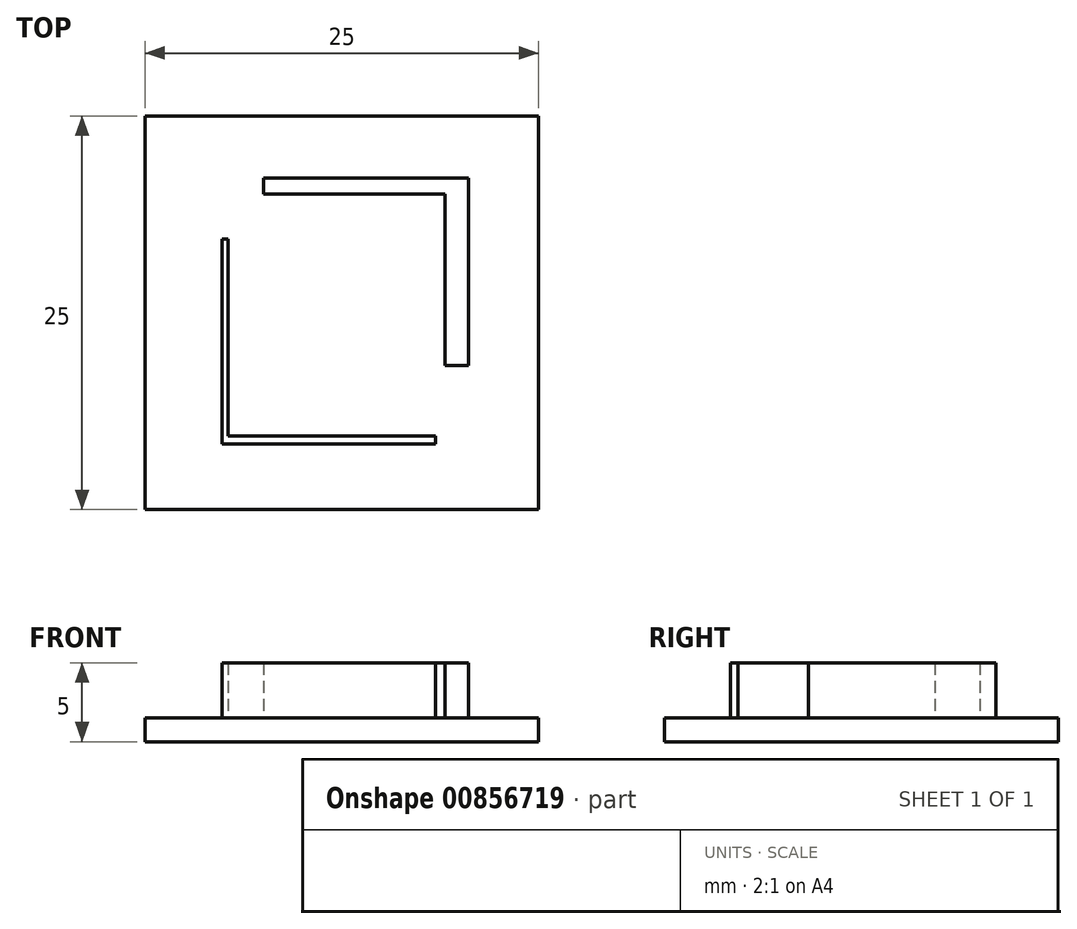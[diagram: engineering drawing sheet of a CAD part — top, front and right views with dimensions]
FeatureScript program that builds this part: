
annotation { "Feature Type Name" : "Feature", "Feature Type Description" : "" }
export const myFeature = defineFeature(function(context is Context, id is Id, definition is map)
    precondition{}
    {
        {
            var Q0;
            Q0=qCreatedBy(makeId("Top.planeOp"),FACE);
            var sketch = newSketch(context, id + "F0", { "sketchPlane" : qUnion([Q0])});
            skLineSegment(sketch, "E0.bottom", {"start": v(-25, 12.5) * mm, "end": v(0, 12.5) * mm});
            skLineSegment(sketch, "E0.top", {"start": v(-25, -12.5) * mm, "end": v(0, -12.5) * mm});
            skLineSegment(sketch, "E0.left", {"start": v(-25, 12.5) * mm, "end": v(-25, -12.5) * mm});
            skLineSegment(sketch, "E0.right", {"start": v(0, 12.5) * mm, "end": v(0, -12.5) * mm});
            skLineSegment(sketch, "E1", {"start": v(-17.46, 8.54) * mm, "end": v(-4.46, 8.54) * mm});
            skLineSegment(sketch, "E2", {"start": v(-4.46, 8.54) * mm, "end": v(-4.46, -3.37) * mm});
            skLineSegment(sketch, "E3", {"start": v(-5.96, -3.37) * mm, "end": v(-5.96, 7.54) * mm});
            skLineSegment(sketch, "E4", {"start": v(-5.96, 7.54) * mm, "end": v(-17.46, 7.54) * mm});
            skLineSegment(sketch, "E5", {"start": v(-17.46, 7.54) * mm, "end": v(-17.46, 8.54) * mm});
            skLineSegment(sketch, "E6", {"start": v(-5.96, -3.37) * mm, "end": v(-4.46, -3.37) * mm});
            skLineSegment(sketch, "E7", {"start": v(-19.72, 4.67) * mm, "end": v(-19.72, -7.83) * mm});
            skLineSegment(sketch, "E8", {"start": v(-19.72, -7.83) * mm, "end": v(-6.56, -7.83) * mm});
            skLineSegment(sketch, "E9", {"start": v(-6.56, -7.83) * mm, "end": v(-6.56, -8.33) * mm});
            skLineSegment(sketch, "E10", {"start": v(-6.56, -8.33) * mm, "end": v(-20.12, -8.33) * mm});
            skLineSegment(sketch, "E11", {"start": v(-20.12, -8.33) * mm, "end": v(-20.12, 4.67) * mm});
            skLineSegment(sketch, "E12", {"start": v(-20.12, 4.67) * mm, "end": v(-19.72, 4.67) * mm});
            skSolve(sketch);
        }
        {
            var Q0;
            Q0=makeQuery(id+"F0.imprint","IMPRINT",FACE,{"disambiguationData":[TD([[makeQuery(id+"F0.imprint","IMPRINT",EDGE,{"derivedFrom":sQuery(id+"F0.wireOp",EDGE,"E1")}),-1.0]])]});
            extrude(context, id + "F1", {"entities" : qUnion([Q0]), "depth" : 5 * mm, "offsetDistance" : 25 * mm});
        }
        {
            var Q0;
            Q0=makeQuery(id+"F0.imprint","IMPRINT",FACE,{"disambiguationData":[TD([[makeQuery(id+"F0.imprint","IMPRINT",EDGE,{"derivedFrom":sQuery(id+"F0.wireOp",EDGE,"E0.bottom")}),-1.0]])]});
            extrude(context, id + "F2", {"entities" : qUnion([Q0]), "operationType" : NewBodyOperationType.ADD, "depth" : 1.5 * mm, "offsetDistance" : 25 * mm});
        }
        {
            var Q0;
            Q0=makeQuery(id+"F0.imprint","IMPRINT",FACE,{"disambiguationData":[TD([[makeQuery(id+"F0.imprint","IMPRINT",EDGE,{"derivedFrom":sQuery(id+"F0.wireOp",EDGE,"E7")}),-1.0]])]});
            extrude(context, id + "F3", {"entities" : qUnion([Q0]), "operationType" : NewBodyOperationType.ADD, "depth" : 5 * mm, "offsetDistance" : 25 * mm});
        }
    });
